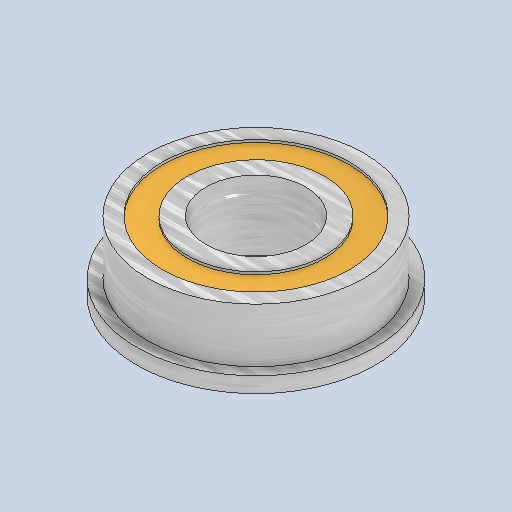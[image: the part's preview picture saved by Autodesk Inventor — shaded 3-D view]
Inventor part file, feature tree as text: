
AUTODESK INVENTOR PART (.ipt)
format: ipt  version: 2024 (Build 280153000, 153)  size: 183,296 bytes
history: native  units: in
note: dims shown in document units (in); Inventor stores cm internally (conversion verified against a paired STEP export)
features: revolve x1
ambient origin geometry x8: Origin, YZ Plane, XZ Plane, XY Plane, X Axis, Y Axis, Z Axis, Center Point
bodies: Solid1 (feature_tree)
feature tree (1):
  revolve  "Revolve1"  [1 undecoded]
note: 1 required parameter value undecoded (feature->parameter linkage not recoverable at this tier; creation-order binding heuristic only, values carry confidence <= 0.55)
